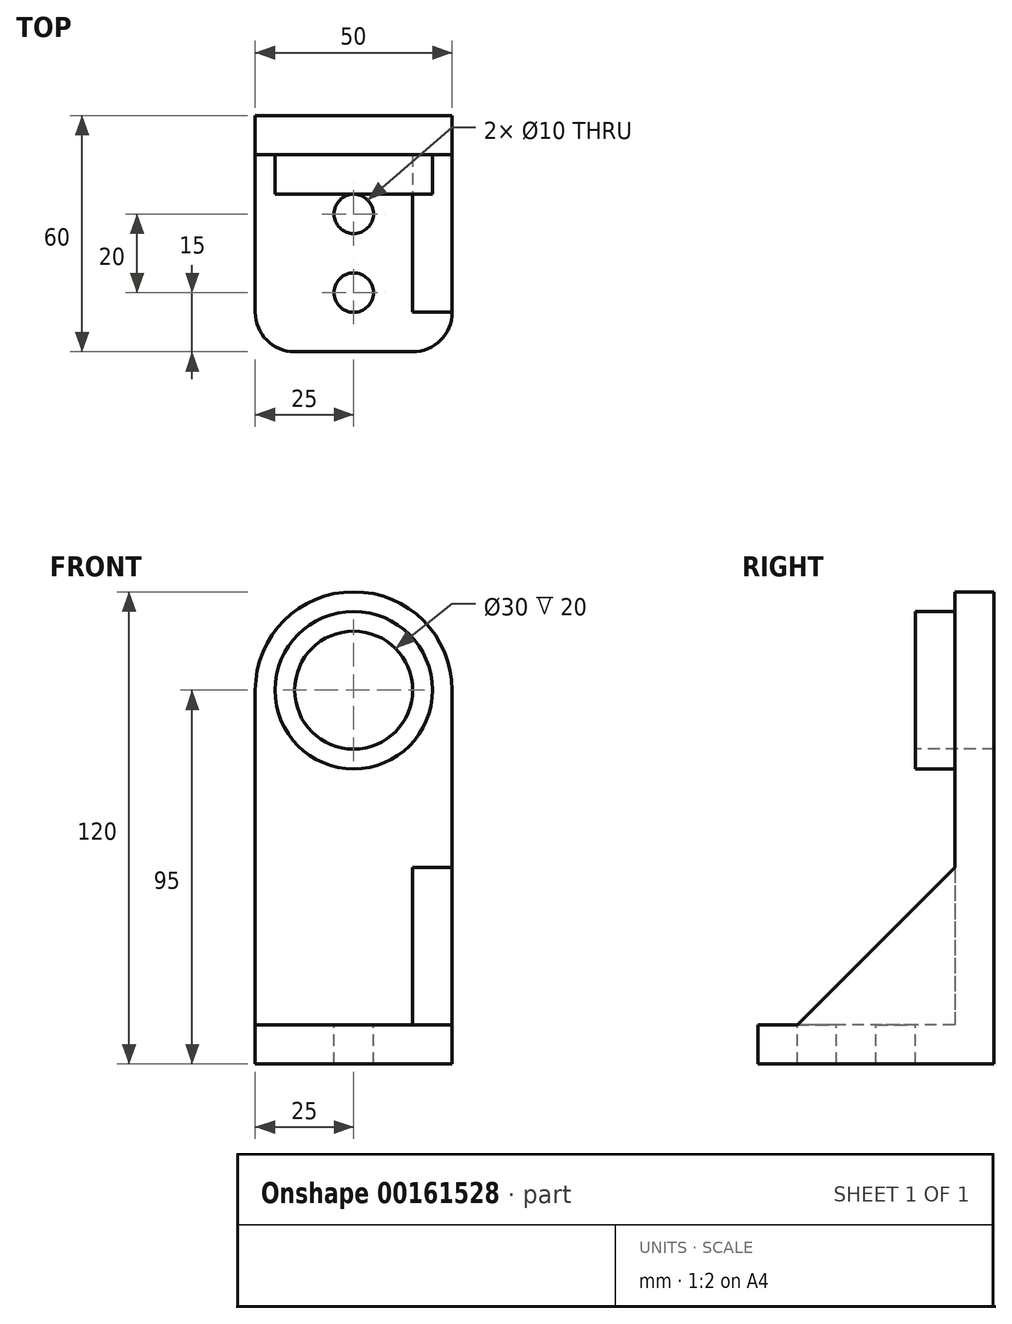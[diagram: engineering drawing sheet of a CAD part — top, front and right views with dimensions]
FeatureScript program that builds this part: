
annotation { "Feature Type Name" : "Feature", "Feature Type Description" : "" }
export const myFeature = defineFeature(function(context is Context, id is Id, definition is map)
    precondition{}
    {
        {
            var Q0;
            Q0=qCreatedBy(makeId("Right.planeOp"),FACE);
            var sketch = newSketch(context, id + "F0", { "sketchPlane" : qUnion([Q0])});
            skLineSegment(sketch, "E0", {"start": v(0, 0) * mm, "end": v(0, 120) * mm});
            skLineSegment(sketch, "E1", {"start": v(0, 120) * mm, "end": v(-10, 120) * mm});
            skLineSegment(sketch, "E2", {"start": v(-10, 120) * mm, "end": v(-10, 10) * mm});
            skLineSegment(sketch, "E3", {"start": v(-10, 10) * mm, "end": v(-60, 10) * mm});
            skLineSegment(sketch, "E4", {"start": v(-60, 10) * mm, "end": v(-60, 0) * mm});
            skLineSegment(sketch, "E5", {"start": v(-60, 0) * mm, "end": v(0, 0) * mm});
            skSolve(sketch);
        }
        {
            var Q0;
            Q0=makeQuery(id+"F0.imprint","IMPRINT",FACE,{"disambiguationData":[TD([[makeQuery(id+"F0.imprint","IMPRINT",EDGE,{"derivedFrom":sQuery(id+"F0.wireOp",EDGE,"E0")}),1.0]])]});
            extrude(context, id + "F1", {"entities" : qUnion([Q0]), "endBound" : BoundingType.SYMMETRIC, "depth" : 50 * mm});
        }
        {
            var Q0;
            Q0=makeQuery(id+"F1.opExtrude","CAP_FACE",FACE,{"disambiguationData":[OSD([sQuery(id+"F0.wireOp",EDGE,"E0"),sQuery(id+"F0.wireOp",EDGE,"E1"),sQuery(id+"F0.wireOp",EDGE,"E2"),sQuery(id+"F0.wireOp",EDGE,"E3"),sQuery(id+"F0.wireOp",EDGE,"E4"),sQuery(id+"F0.wireOp",EDGE,"E5")])],"isStart":false});
            var sketch = newSketch(context, id + "F2", { "sketchPlane" : qUnion([Q0])});
            skLineSegment(sketch, "E6", {"start": v(-10, 10) * mm, "end": v(-10, 50) * mm});
            skLineSegment(sketch, "E7", {"start": v(-10, 50) * mm, "end": v(-50, 10) * mm});
            skLineSegment(sketch, "E8", {"start": v(-50, 10) * mm, "end": v(-10, 10) * mm});
            skSolve(sketch);
        }
        {
            var Q0;
            Q0=makeQuery(id+"F2.imprint","IMPRINT",FACE,{"disambiguationData":[TD([[makeQuery(id+"F2.imprint","IMPRINT",EDGE,{"derivedFrom":sQuery(id+"F2.wireOp",EDGE,"E6")}),-1.0]])]});
            extrude(context, id + "F3", {"entities" : qUnion([Q0]), "operationType" : NewBodyOperationType.ADD, "oppositeDirection" : true, "depth" : 10 * mm});
        }
        {
            var Q0;
            Q0=makeQuery(id+"F1.opExtrude","SWEPT_FACE",FACE,{"disambiguationData":[OSD([sQuery(id+"F0.wireOp",EDGE,"E2")])]});
            var sketch = newSketch(context, id + "F4", { "sketchPlane" : qUnion([Q0])});
            skCircle(sketch, "E9", {"center": v(0, 95) * mm, "radius": 20 * mm});
            skSolve(sketch);
        }
        {
            var Q0;
            Q0=makeQuery(id+"F4.imprint","IMPRINT",FACE,{"disambiguationData":[TD([[makeQuery(id+"F4.imprint","IMPRINT",EDGE,{"derivedFrom":sQuery(id+"F4.wireOp",EDGE,"E9")}),1.0]])]});
            extrude(context, id + "F5", {"entities" : qUnion([Q0]), "operationType" : NewBodyOperationType.ADD, "depth" : 10 * mm});
        }
        {
            var Q0;
            Q0=makeQuery(id+"F1.opExtrude","CAP_EDGE",EDGE,{"disambiguationData":[OSD([sQuery(id+"F0.wireOp",EDGE,"E1")])],"isStart":true});
            var Q1;
            Q1=makeQuery(id+"F1.opExtrude","CAP_EDGE",EDGE,{"disambiguationData":[OSD([sQuery(id+"F0.wireOp",EDGE,"E1")])],"isStart":false});
            fillet(context, id + "F6", {"entities" : qUnion([Q0, Q1]), "radius" : 25 * mm, "tangentPropagation" : true, "allowEdgeOverflow" : false});
        }
        {
            var Q0;
            Q0=makeQuery(id+"F5.opExtrude","CAP_FACE",FACE,{"disambiguationData":[OSD([sQuery(id+"F4.wireOp",EDGE,"E9")])],"isStart":false});
            var sketch = newSketch(context, id + "F7", { "sketchPlane" : qUnion([Q0])});
            skPoint(sketch, "E10", {"position": v(0, 95) * mm});
            skSolve(sketch);
        }
        {
            var Q0;
            Q0=sQuery(id+"F7.wireOp",VERTEX,"E10");
            var Q1;
            Q1=makeQuery(id+"F1.opExtrude","SWEPT_BODY",BODY,{"disambiguationData":[OSD([sQuery(id+"F0.wireOp",EDGE,"E0"),sQuery(id+"F0.wireOp",EDGE,"E1"),sQuery(id+"F0.wireOp",EDGE,"E2"),sQuery(id+"F0.wireOp",EDGE,"E3"),sQuery(id+"F0.wireOp",EDGE,"E4"),sQuery(id+"F0.wireOp",EDGE,"E5")])]});
            hole(context, id + "F8", {"style" : HoleStyle.SIMPLE, "endStyle" : HoleEndStyle.THROUGH, "holeDiameter" : 30 * mm, "locations" : qUnion([Q0]), "scope" : qUnion([Q1]), "isTappedThrough" : true});
        }
        {
            var Q0;
            Q0=makeQuery(id+"F1.opExtrude","CAP_EDGE",EDGE,{"disambiguationData":[OSD([sQuery(id+"F0.wireOp",EDGE,"E4")])],"isStart":true});
            var Q1;
            Q1=makeQuery(id+"F1.opExtrude","CAP_EDGE",EDGE,{"disambiguationData":[OSD([sQuery(id+"F0.wireOp",EDGE,"E4")])],"isStart":false});
            fillet(context, id + "F9", {"entities" : qUnion([Q0, Q1]), "radius" : 10 * mm, "tangentPropagation" : true, "allowEdgeOverflow" : false});
        }
        {
            var Q0;
            Q0=makeQuery(id+"F1.opExtrude","SWEPT_FACE",FACE,{"disambiguationData":[OSD([sQuery(id+"F0.wireOp",EDGE,"E3")])]});
            var sketch = newSketch(context, id + "F10", { "sketchPlane" : qUnion([Q0])});
            skPoint(sketch, "E11", {"position": v(0, -25) * mm});
            skPoint(sketch, "E12", {"position": v(0, -45) * mm});
            skSolve(sketch);
        }
        {
            var Q0;
            Q0=sQuery(id+"F10.wireOp",VERTEX,"E11");
            var Q1;
            Q1=sQuery(id+"F10.wireOp",VERTEX,"E12");
            var Q2;
            Q2=makeQuery(id+"F1.opExtrude","SWEPT_BODY",BODY,{"disambiguationData":[OSD([sQuery(id+"F0.wireOp",EDGE,"E0"),sQuery(id+"F0.wireOp",EDGE,"E1"),sQuery(id+"F0.wireOp",EDGE,"E2"),sQuery(id+"F0.wireOp",EDGE,"E3"),sQuery(id+"F0.wireOp",EDGE,"E4"),sQuery(id+"F0.wireOp",EDGE,"E5")])]});
            hole(context, id + "F11", {"style" : HoleStyle.SIMPLE, "endStyle" : HoleEndStyle.THROUGH, "holeDiameter" : 10 * mm, "locations" : qUnion([Q0, Q1]), "scope" : qUnion([Q2]), "isTappedThrough" : true});
        }
    });
